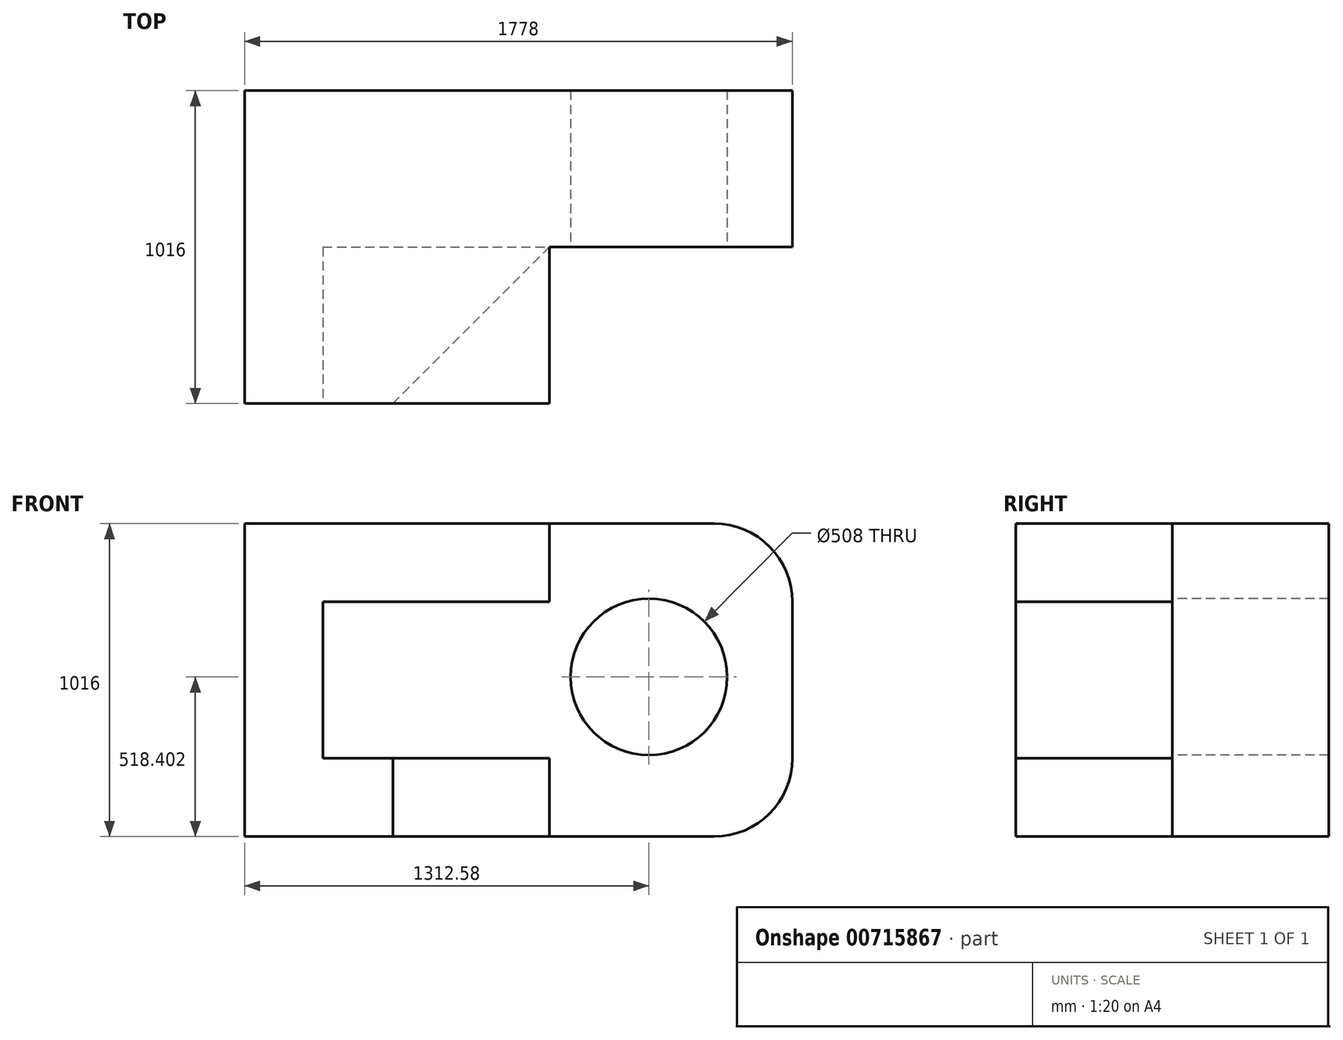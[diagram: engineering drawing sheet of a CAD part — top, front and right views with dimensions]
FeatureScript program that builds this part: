
annotation { "Feature Type Name" : "Feature", "Feature Type Description" : "" }
export const myFeature = defineFeature(function(context is Context, id is Id, definition is map)
    precondition{}
    {
        {
            var Q0;
            Q0=qCreatedBy(makeId("Top.planeOp"),FACE);
            var sketch = newSketch(context, id + "F0", { "sketchPlane" : qUnion([Q0])});
            skLineSegment(sketch, "E0.bottom", {"start": v(-755.55, 513.04) * mm, "end": v(1022.45, 513.04) * mm});
            skLineSegment(sketch, "E0.top", {"start": v(-755.55, -502.96) * mm, "end": v(1022.45, -502.96) * mm});
            skLineSegment(sketch, "E0.left", {"start": v(-755.55, 513.04) * mm, "end": v(-755.55, -502.96) * mm});
            skLineSegment(sketch, "E0.right", {"start": v(1022.45, 513.04) * mm, "end": v(1022.45, -502.96) * mm});
            skSolve(sketch);
        }
        {
            var Q0;
            Q0 = qSketchRegion(id + "F0", true);
            extrude(context, id + "F1", {"entities" : qUnion([Q0]), "depth" : 1016 * mm, "offsetDistance" : 25.4 * mm});
        }
        {
            var Q0;
            Q0=makeQuery(id+"F1.opExtrude","SWEPT_FACE",FACE,{"disambiguationData":[OSD([sQuery(id+"F0.wireOp",EDGE,"E0.top")])]});
            var sketch = newSketch(context, id + "F2", { "sketchPlane" : qUnion([Q0])});
            skLineSegment(sketch, "E1.bottom", {"start": v(-501.55, 762) * mm, "end": v(260.45, 762) * mm});
            skLineSegment(sketch, "E1.top", {"start": v(-501.55, 254) * mm, "end": v(260.45, 254) * mm});
            skLineSegment(sketch, "E1.left", {"start": v(-501.55, 762) * mm, "end": v(-501.55, 254) * mm});
            skLineSegment(sketch, "E1.right", {"start": v(260.45, 762) * mm, "end": v(260.45, 254) * mm});
            skSolve(sketch);
        }
        {
            var Q0;
            Q0=makeQuery(id+"F2.imprint","IMPRINT",FACE,{"disambiguationData":[TD([[makeQuery(id+"F2.imprint","IMPRINT",EDGE,{"derivedFrom":sQuery(id+"F2.wireOp",EDGE,"E1.bottom")}),-1.0]])]});
            extrude(context, id + "F3", {"entities" : qUnion([Q0]), "operationType" : NewBodyOperationType.REMOVE, "oppositeDirection" : true, "depth" : 508 * mm, "offsetDistance" : 25.4 * mm});
        }
        {
            var Q0;
            Q0=makeQuery(id+"F1.opExtrude","SWEPT_FACE",FACE,{"disambiguationData":[OSD([sQuery(id+"F0.wireOp",EDGE,"E0.top")])]});
            var sketch = newSketch(context, id + "F4", { "sketchPlane" : qUnion([Q0])});
            skLineSegment(sketch, "E2.bottom", {"start": v(233.68, 1016) * mm, "end": v(1022.45, 1016) * mm});
            skLineSegment(sketch, "E2.top", {"start": v(233.68, 0) * mm, "end": v(1022.45, 0) * mm});
            skLineSegment(sketch, "E2.left", {"start": v(233.68, 1016) * mm, "end": v(233.68, 0) * mm});
            skLineSegment(sketch, "E2.right", {"start": v(1022.45, 1016) * mm, "end": v(1022.45, 0) * mm});
            skSolve(sketch);
        }
        {
            var Q0;
            {var subQ5=makeQuery(id+"F3.boolean.opBoolean","COPY",EDGE,{"derivedFrom":makeQuery(id+"F3.opExtrude","CAP_EDGE",EDGE,{"disambiguationData":[OSD([sQuery(id+"F2.wireOp",EDGE,"E1.right")])],"isStart":true})});Q0=makeQuery(id+"F4.imprint","IMPRINT",FACE,{"disambiguationData":[TD([[makeQuery(id+"F4.imprint","IMPRINT",EDGE,{"derivedFrom":subQ5}),-1.0]])]});}
            var Q1;
            {var subQ5=sQuery(id+"F4.wireOp",EDGE,"E2.bottom");Q1=makeQuery(id+"F4.imprint","IMPRINT",FACE,{"disambiguationData":[TD([[makeQuery(id+"F4.imprint","IMPRINT",EDGE,{"derivedFrom":subQ5}),-1.0]])]});}
            extrude(context, id + "F5", {"entities" : qUnion([Q0, Q1]), "operationType" : NewBodyOperationType.REMOVE, "oppositeDirection" : true, "depth" : 508 * mm, "offsetDistance" : 25.4 * mm});
        }
        {
            var Q0;
            Q0=makeQuery(id+"F1.opExtrude","CAP_EDGE",EDGE,{"disambiguationData":[OSD([sQuery(id+"F0.wireOp",EDGE,"E0.right")])],"isStart":false});
            fillet(context, id + "F6", {"entities" : qUnion([Q0]), "radius" : 254 * mm, "tangentPropagation" : true, "allowEdgeOverflow" : false});
        }
        {
            var Q0;
            Q0=makeQuery(id+"F1.opExtrude","CAP_EDGE",EDGE,{"disambiguationData":[OSD([sQuery(id+"F0.wireOp",EDGE,"E0.right")])],"isStart":true});
            fillet(context, id + "F7", {"entities" : qUnion([Q0]), "radius" : 254 * mm, "tangentPropagation" : true, "allowEdgeOverflow" : false});
        }
        {
            var Q0;
            Q0=makeQuery(id+"F5.boolean.opBoolean","MERGE",FACE,{"derivedFrom":[makeQuery(id+"F3.boolean.opBoolean","COPY",FACE,{"derivedFrom":makeQuery(id+"F3.opExtrude","CAP_FACE",FACE,{"disambiguationData":[OSD([sQuery(id+"F2.wireOp",EDGE,"E1.bottom"),sQuery(id+"F2.wireOp",EDGE,"E1.top"),sQuery(id+"F2.wireOp",EDGE,"E1.left"),sQuery(id+"F2.wireOp",EDGE,"E1.right")])],"isStart":false})}),makeQuery(id+"F5.opExtrude","CAP_FACE",FACE,{"disambiguationData":[OSD([sQuery(id+"F4.wireOp",EDGE,"E2.bottom"),sQuery(id+"F4.wireOp",EDGE,"E2.top"),sQuery(id+"F4.wireOp",EDGE,"E2.left"),sQuery(id+"F4.wireOp",EDGE,"E2.right")])],"isStart":false})]});
            var sketch = newSketch(context, id + "F8", { "sketchPlane" : qUnion([Q0])});
            skCircle(sketch, "E3", {"center": v(557.03, 518.4) * mm, "radius": 254 * mm});
            skSolve(sketch);
        }
        {
            var Q0;
            Q0=makeQuery(id+"F8.imprint","IMPRINT",FACE,{"disambiguationData":[TD([[makeQuery(id+"F8.imprint","IMPRINT",EDGE,{"derivedFrom":sQuery(id+"F8.wireOp",EDGE,"E3")}),1.0]])]});
            extrude(context, id + "F9", {"entities" : qUnion([Q0]), "operationType" : NewBodyOperationType.REMOVE, "oppositeDirection" : true, "depth" : 508 * mm, "offsetDistance" : 25.4 * mm});
        }
        {
            var Q0;
            Q0=makeQuery(id+"F1.opExtrude","CAP_FACE",FACE,{"disambiguationData":[OSD([sQuery(id+"F0.wireOp",EDGE,"E0.bottom"),sQuery(id+"F0.wireOp",EDGE,"E0.top"),sQuery(id+"F0.wireOp",EDGE,"E0.left"),sQuery(id+"F0.wireOp",EDGE,"E0.right")])],"isStart":true});
            var sketch = newSketch(context, id + "F10", { "sketchPlane" : qUnion([Q0])});
            skLineSegment(sketch, "E4", {"start": v(233.68, 502.96) * mm, "end": v(-274.32, 502.96) * mm});
            skLineSegment(sketch, "E5", {"start": v(-274.32, 502.96) * mm, "end": v(233.68, -5.04) * mm});
            skLineSegment(sketch, "E6", {"start": v(233.68, -5.04) * mm, "end": v(233.68, 502.96) * mm});
            skSolve(sketch);
        }
        {
            var Q0;
            Q0=makeQuery(id+"F10.imprint","IMPRINT",FACE,{"disambiguationData":[TD([[makeQuery(id+"F10.imprint","IMPRINT",EDGE,{"derivedFrom":sQuery(id+"F10.wireOp",EDGE,"E4")}),-1.0]])]});
            extrude(context, id + "F11", {"entities" : qUnion([Q0]), "operationType" : NewBodyOperationType.REMOVE, "oppositeDirection" : true, "depth" : 254 * mm, "offsetDistance" : 25.4 * mm});
        }
    });
